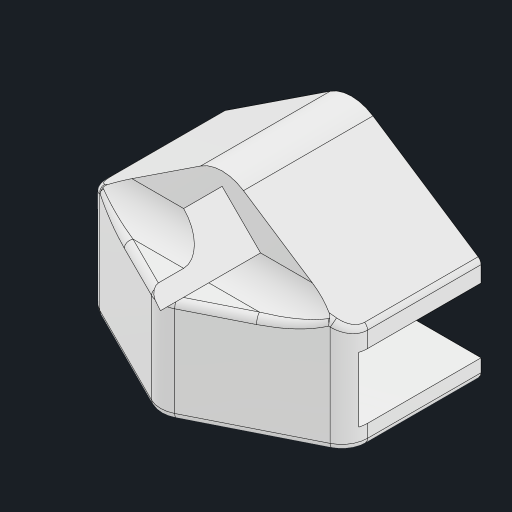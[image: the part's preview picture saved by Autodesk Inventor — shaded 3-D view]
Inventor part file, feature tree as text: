
AUTODESK INVENTOR PART (.ipt)
format: ipt  version: 2023 (Build 270158000, 158)  size: 271,360 bytes
history: native  units: mm
features: extrude x5, sketch x5, projected_geometry x5, fillet x3, other x2
ambient origin geometry x8: Origin, YZ Plane, XZ Plane, XY Plane, X Axis, Y Axis, Z Axis, Center Point
bodies: Body1 (feature_tree)
feature tree (20):
  other  "ソリッド1"
  extrude  "押し出し1"  Depth=20.0mm
  extrude  "押し出し2"  Depth=5.0mm
  extrude  "押し出し3"  Depth=15.0mm
  extrude  "押し出し4"  Depth=1.5mm TaperAngle=0.0deg
  fillet  "フィレット2"  Radius=300.0mm
  fillet  "フィレット3"  Radius=40.0mm
  fillet  "フィレット4"  Radius=3.0mm
  extrude  "押し出し5"  Depth=5.0mm TaperAngle=0.0deg
  other  "作業平面1"
  sketch  "スケッチ1"
  sketch  "スケッチ2"
  projected_geometry  "投影ループ1"
  sketch  "スケッチ3"
  projected_geometry  "投影ループ2"
  projected_geometry  "投影ループ3"
  sketch  "スケッチ4"
  projected_geometry  "投影ループ4"
  sketch  "スケッチ5"
  projected_geometry  "投影ループ5"
